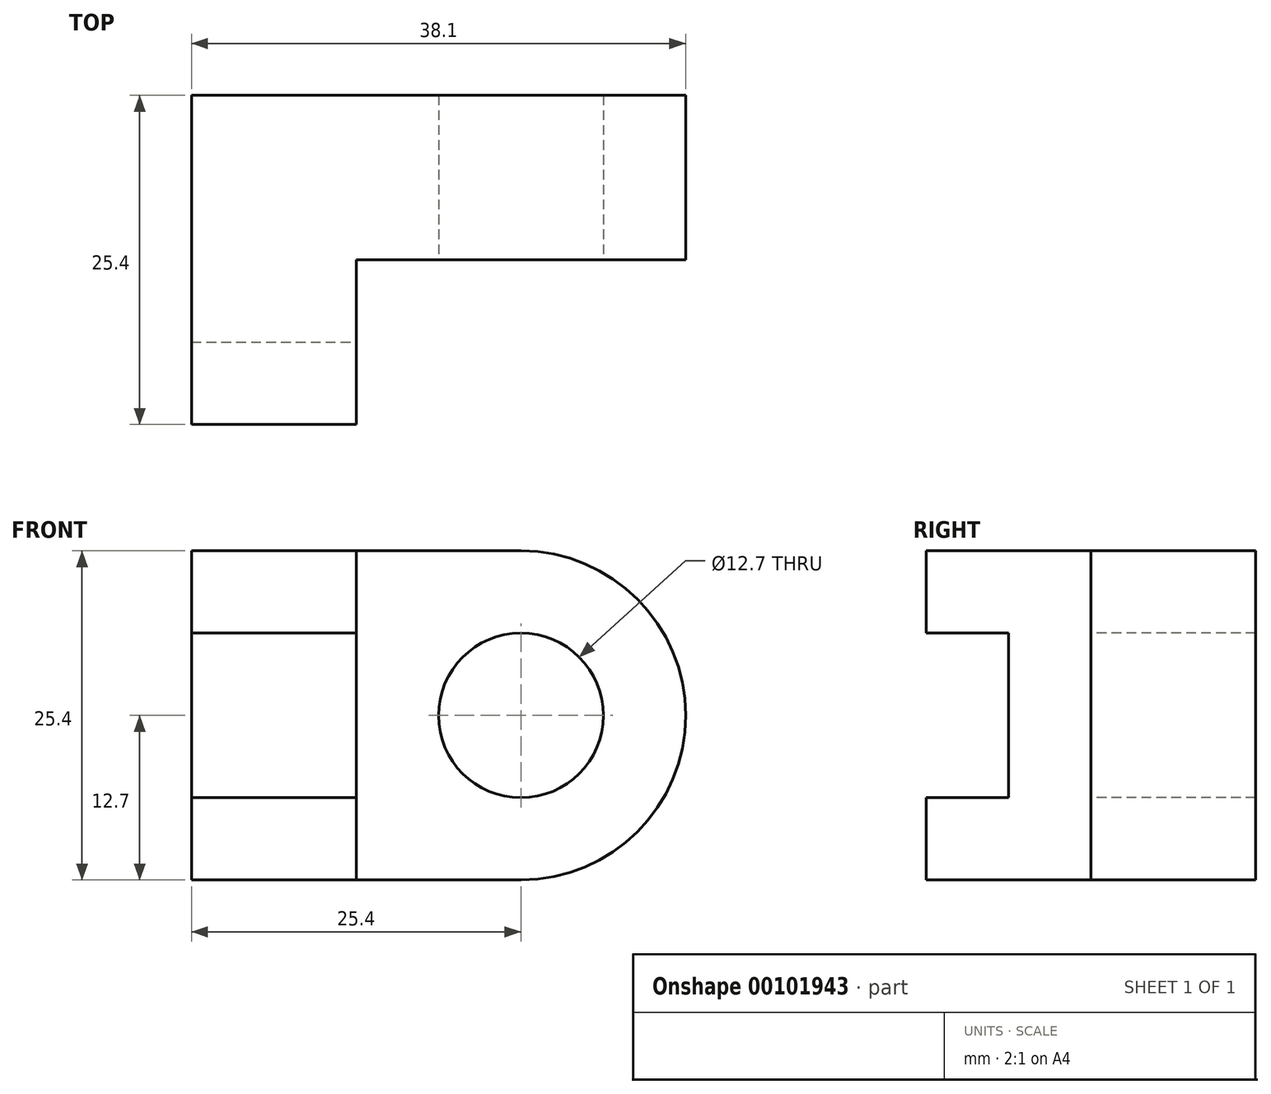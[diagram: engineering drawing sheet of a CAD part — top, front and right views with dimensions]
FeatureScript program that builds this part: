
annotation { "Feature Type Name" : "Feature", "Feature Type Description" : "" }
export const myFeature = defineFeature(function(context is Context, id is Id, definition is map)
    precondition{}
    {
        {
            var Q0;
            Q0=qCreatedBy(makeId("Front.planeOp"),FACE);
            var sketch = newSketch(context, id + "F0", { "sketchPlane" : qUnion([Q0])});
            skLineSegment(sketch, "E0.bottom", {"start": v(0, 0) * mm, "end": v(-12.7, 0) * mm});
            skLineSegment(sketch, "E0.top", {"start": v(0, 25.4) * mm, "end": v(-12.7, 25.4) * mm});
            skLineSegment(sketch, "E0.left", {"start": v(0, 0) * mm, "end": v(0, 25.4) * mm});
            skLineSegment(sketch, "E0.right", {"start": v(-12.7, 0) * mm, "end": v(-12.7, 25.4) * mm});
            skLineSegment(sketch, "E1.bottom", {"start": v(0, 0) * mm, "end": v(12.7, 0) * mm});
            skLineSegment(sketch, "E1.top", {"start": v(0, 25.4) * mm, "end": v(12.7, 25.4) * mm});
            skLineSegment(sketch, "E1.right", {"start": v(12.7, 0) * mm, "end": v(12.7, 25.4) * mm});
            skArc(sketch, "E2", {"start": v(12.7, 0) * mm, "mid": v(25.4, 12.7) * mm, "end": v(12.7, 25.4) * mm});
            skSolve(sketch);
        }
        {
            var Q0;
            Q0 = qSketchRegion(id + "F0", true);
            extrude(context, id + "F1", {"entities" : qUnion([Q0]), "endBound" : BoundingType.SYMMETRIC, "depth" : 25.4 * mm});
        }
        {
            var Q0;
            Q0=makeQuery(id+"F1.opExtrude","CAP_FACE",FACE,{"disambiguationData":[OSD([sQuery(id+"F0.wireOp",EDGE,"E0.bottom"),sQuery(id+"F0.wireOp",EDGE,"E0.top"),sQuery(id+"F0.wireOp",EDGE,"E0.right"),sQuery(id+"F0.wireOp",EDGE,"E1.bottom"),sQuery(id+"F0.wireOp",EDGE,"E1.top"),sQuery(id+"F0.wireOp",EDGE,"E2")])],"isStart":false});
            var sketch = newSketch(context, id + "F2", { "sketchPlane" : qUnion([Q0])});
            skLineSegment(sketch, "E3.bottom", {"start": v(-12.7, 19.05) * mm, "end": v(0, 19.05) * mm});
            skLineSegment(sketch, "E3.top", {"start": v(-12.7, 6.35) * mm, "end": v(0, 6.35) * mm});
            skLineSegment(sketch, "E3.left", {"start": v(-12.7, 19.05) * mm, "end": v(-12.7, 6.35) * mm});
            skLineSegment(sketch, "E3.right", {"start": v(0, 19.05) * mm, "end": v(0, 6.35) * mm});
            skSolve(sketch);
        }
        {
            var Q0;
            Q0=makeQuery(id+"F2.imprint","IMPRINT",FACE,{"disambiguationData":[TD([[makeQuery(id+"F2.imprint","IMPRINT",EDGE,{"derivedFrom":sQuery(id+"F2.wireOp",EDGE,"E3.bottom")}),-1.0]])]});
            extrude(context, id + "F3", {"entities" : qUnion([Q0]), "operationType" : NewBodyOperationType.REMOVE, "endBound" : BoundingType.SYMMETRIC, "oppositeDirection" : true, "depth" : 12.7 * mm});
        }
        {
            var Q0;
            Q0=makeQuery(id+"F1.opExtrude","CAP_FACE",FACE,{"disambiguationData":[OSD([sQuery(id+"F0.wireOp",EDGE,"E0.bottom"),sQuery(id+"F0.wireOp",EDGE,"E0.top"),sQuery(id+"F0.wireOp",EDGE,"E0.right"),sQuery(id+"F0.wireOp",EDGE,"E1.bottom"),sQuery(id+"F0.wireOp",EDGE,"E1.top"),sQuery(id+"F0.wireOp",EDGE,"E2")])],"isStart":false});
            var sketch = newSketch(context, id + "F4", { "sketchPlane" : qUnion([Q0])});
            skCircle(sketch, "E4", {"center": v(12.7, 12.7) * mm, "radius": 6.35 * mm});
            skSolve(sketch);
        }
        {
            var Q0;
            Q0=makeQuery(id+"F4.imprint","IMPRINT",FACE,{"disambiguationData":[TD([[makeQuery(id+"F4.imprint","IMPRINT",EDGE,{"derivedFrom":sQuery(id+"F4.wireOp",EDGE,"E4")}),1.0]])]});
            extrude(context, id + "F5", {"entities" : qUnion([Q0]), "operationType" : NewBodyOperationType.REMOVE, "endBound" : BoundingType.THROUGH_ALL, "oppositeDirection" : true, "depth" : 25.4 * mm});
        }
        {
            var Q0;
            Q0=makeQuery(id+"F1.opExtrude","CAP_FACE",FACE,{"disambiguationData":[OSD([sQuery(id+"F0.wireOp",EDGE,"E0.bottom"),sQuery(id+"F0.wireOp",EDGE,"E0.top"),sQuery(id+"F0.wireOp",EDGE,"E0.right"),sQuery(id+"F0.wireOp",EDGE,"E1.bottom"),sQuery(id+"F0.wireOp",EDGE,"E1.top"),sQuery(id+"F0.wireOp",EDGE,"E2")])],"isStart":false});
            var sketch = newSketch(context, id + "F6", { "sketchPlane" : qUnion([Q0])});
            skLineSegment(sketch, "E5.bottom", {"start": v(0, 25.4) * mm, "end": v(12.7, 25.4) * mm});
            skLineSegment(sketch, "E5.top", {"start": v(0, 0) * mm, "end": v(12.7, 0) * mm});
            skLineSegment(sketch, "E5.left", {"start": v(0, 25.4) * mm, "end": v(0, 0) * mm});
            skLineSegment(sketch, "E5.right", {"start": v(12.7, 25.4) * mm, "end": v(12.7, 0) * mm});
            skSolve(sketch);
        }
        {
            var Q0;
            Q0 = qSketchRegion(id + "F6", true);
            extrude(context, id + "F7", {"entities" : qUnion([Q0]), "operationType" : NewBodyOperationType.REMOVE, "oppositeDirection" : true, "depth" : 12.7 * mm});
        }
        {
            var Q0;
            {var subQ0=sQuery(id+"F0.wireOp",EDGE,"E2");Q0=makeQuery(id+"F7.boolean.opBoolean","SPLIT",FACE,{"disambiguationData":[TD([makeQuery(id+"F1.opExtrude","SWEPT_FACE",FACE,{"disambiguationData":[OSD([subQ0])]})])],"derivedFrom":makeQuery(id+"F1.opExtrude","CAP_FACE",FACE,{"disambiguationData":[OSD([sQuery(id+"F0.wireOp",EDGE,"E0.bottom"),sQuery(id+"F0.wireOp",EDGE,"E0.top"),sQuery(id+"F0.wireOp",EDGE,"E0.right"),sQuery(id+"F0.wireOp",EDGE,"E1.bottom"),sQuery(id+"F0.wireOp",EDGE,"E1.top"),subQ0])],"isStart":false})});}
            var sketch = newSketch(context, id + "F8", { "sketchPlane" : qUnion([Q0])});
            skArc(sketch, "E6", {"start": v(12.7, 0) * mm, "mid": v(25.4, 12.7) * mm, "end": v(12.7, 25.4) * mm});
            skSolve(sketch);
        }
        {
            var Q0;
            Q0=makeQuery(id+"F8.imprint","IMPRINT",FACE,{"disambiguationData":[TD([[makeQuery(id+"F8.imprint","IMPRINT",EDGE,{"derivedFrom":sQuery(id+"F8.wireOp",EDGE,"E6")}),1.0]])]});
            extrude(context, id + "F9", {"entities" : qUnion([Q0]), "operationType" : NewBodyOperationType.REMOVE, "oppositeDirection" : true, "depth" : 12.7 * mm});
        }
    });
